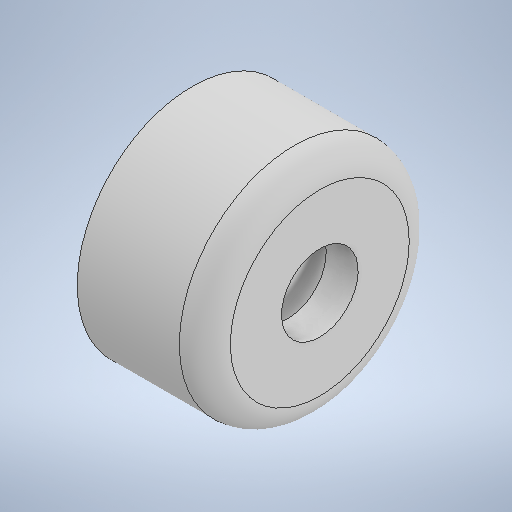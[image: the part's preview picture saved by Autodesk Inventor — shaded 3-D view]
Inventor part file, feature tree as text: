
AUTODESK INVENTOR PART (.ipt)
format: ipt  version: 2025.1 (Build 291241000, 241)  size: 267,776 bytes
history: native  units: mm
features: sketch x2, revolve x1, thread x1, hole x1, fillet x1
ambient origin geometry x8: Origin, YZ Plane, XZ Plane, XY Plane, X Axis, Y Axis, Z Axis, Center Point
bodies: Solid1 (feature_tree)
feature tree (6):
  revolve  "Revolution1"  [1 undecoded]
  thread  "Thread1"  [1 undecoded]
  hole  "Hole1"  [1 undecoded]
  fillet  "Fillet1"  Radius=2.0mm
  sketch  "Sketch1"  dims[d0=45.0deg d1=18.0mm d2=12.0mm]
  sketch  "Sketch2"  dims[d3=2.5mm d4=10.0mm d5=2.0mm d6=90.0deg d7=5.5mm d8=0.0mm d9=6.0mm d10=6.0mm d11=7.0mm d12=2.0mm d13=90.0deg d14=8.0mm d15=0.0mm d16=2.0mm]
note: 3 required parameter values undecoded (feature->parameter linkage not recoverable at this tier; creation-order binding heuristic only, values carry confidence <= 0.55)